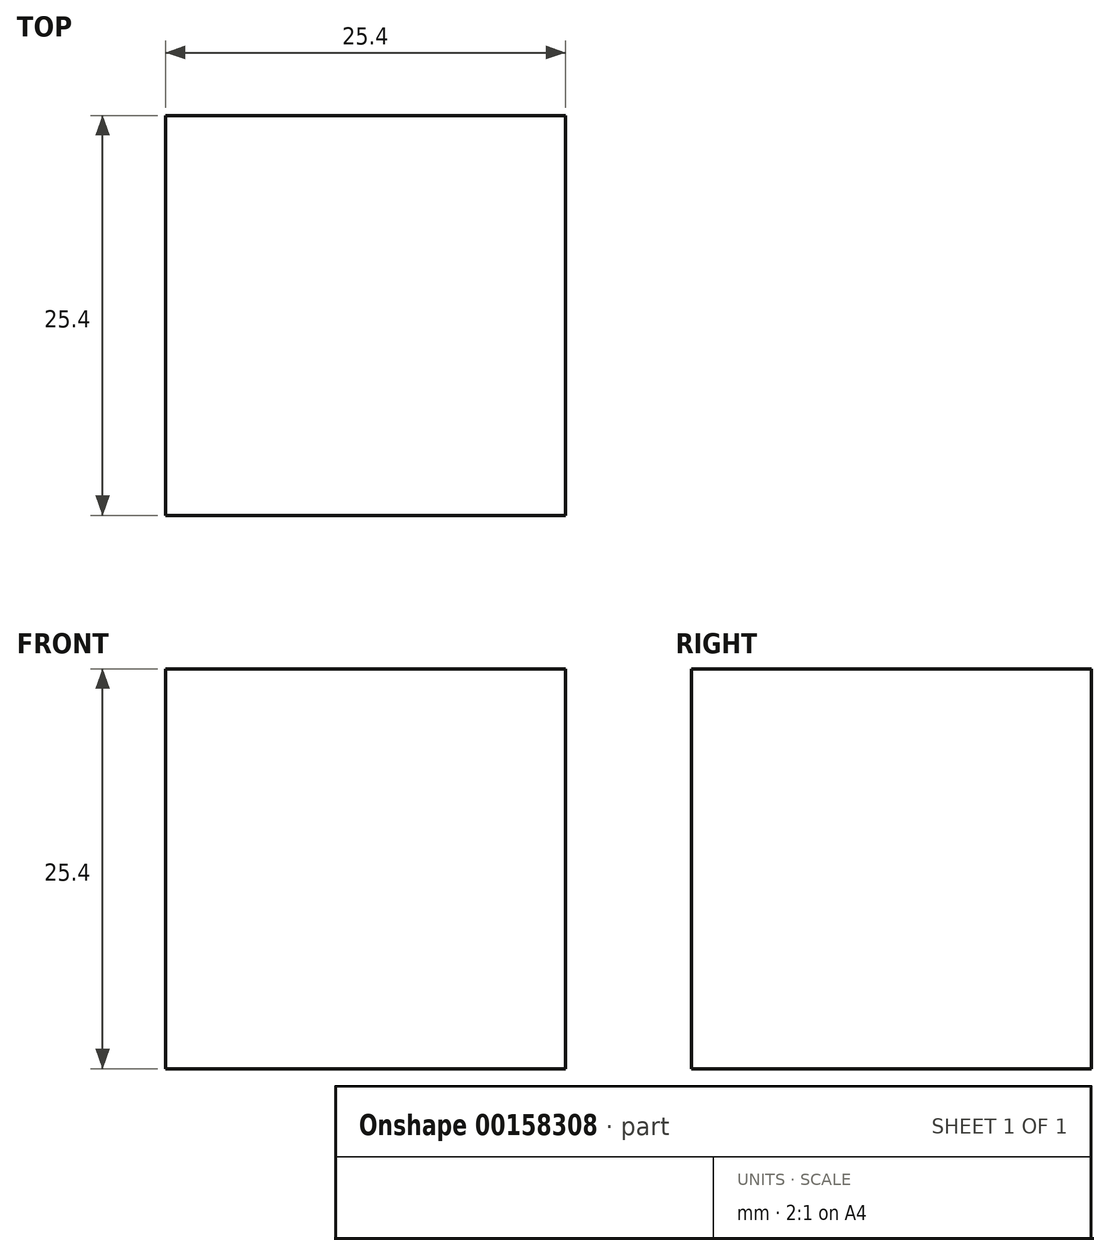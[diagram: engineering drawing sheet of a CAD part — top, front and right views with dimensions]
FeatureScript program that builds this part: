
annotation { "Feature Type Name" : "Feature", "Feature Type Description" : "" }
export const myFeature = defineFeature(function(context is Context, id is Id, definition is map)
    precondition{}
    {
        {
            var Q0;
            Q0=qCreatedBy(makeId("Top.planeOp"),FACE);
            var sketch = newSketch(context, id + "F0", { "sketchPlane" : qUnion([Q0])});
            skLineSegment(sketch, "E0.bottom", {"start": v(12.7, 12.7) * mm, "end": v(-12.7, 12.7) * mm});
            skLineSegment(sketch, "E0.top", {"start": v(12.7, -12.7) * mm, "end": v(-12.7, -12.7) * mm});
            skLineSegment(sketch, "E0.left", {"start": v(12.7, 12.7) * mm, "end": v(12.7, -12.7) * mm});
            skLineSegment(sketch, "E0.right", {"start": v(-12.7, 12.7) * mm, "end": v(-12.7, -12.7) * mm});
            skPoint(sketch, "E0.middle", {"position": v(0, 0) * mm});
            skSolve(sketch);
        }
        {
            var Q0;
            Q0=makeQuery(id+"F0.imprint","IMPRINT",FACE,{"disambiguationData":[TD([[makeQuery(id+"F0.imprint","IMPRINT",EDGE,{"derivedFrom":sQuery(id+"F0.wireOp",EDGE,"E0.bottom")}),1.0]])]});
            extrude(context, id + "F1", {"entities" : qUnion([Q0]), "endBound" : BoundingType.SYMMETRIC, "depth" : 25.4 * mm});
        }
    });
